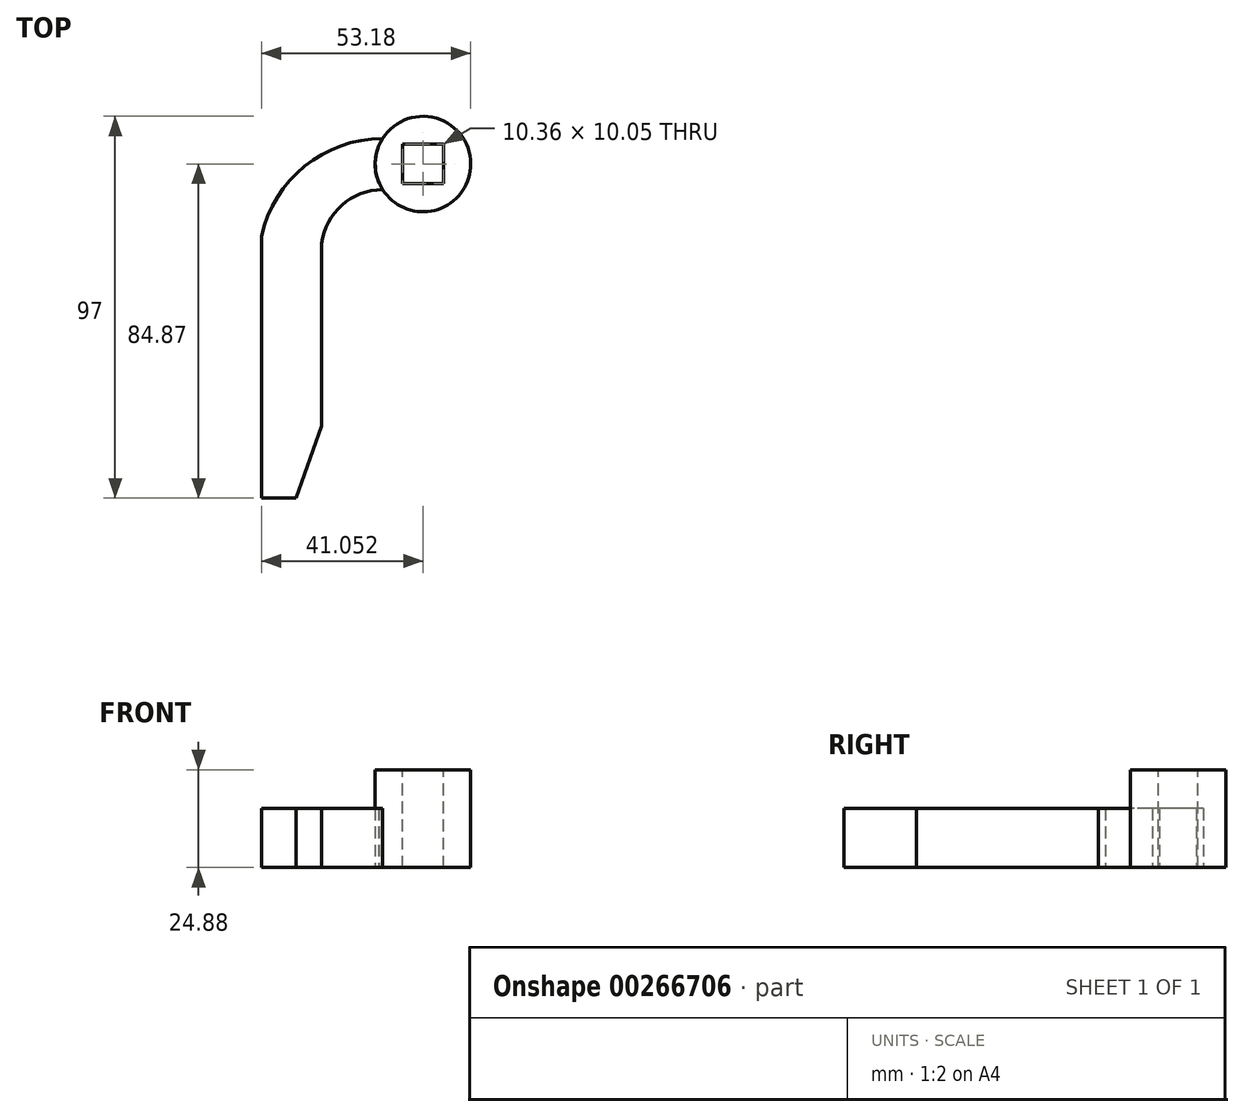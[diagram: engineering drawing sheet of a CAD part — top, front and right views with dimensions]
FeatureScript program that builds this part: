
annotation { "Feature Type Name" : "Feature", "Feature Type Description" : "" }
export const myFeature = defineFeature(function(context is Context, id is Id, definition is map)
    precondition{}
    {
        {
            var Q0;
            Q0=qCreatedBy(makeId("Top.planeOp"),FACE);
            var sketch = newSketch(context, id + "F0", { "sketchPlane" : qUnion([Q0])});
            skCircle(sketch, "E0", {"center": v(50.95, 0) * mm, "radius": 12.13 * mm});
            skSolve(sketch);
        }
        {
            var Q0;
            Q0=qCreatedBy(makeId("Top.planeOp"),FACE);
            var sketch = newSketch(context, id + "F1", { "sketchPlane" : qUnion([Q0])});
            skLineSegment(sketch, "E1.bottom", {"start": v(40.74, 6.47) * mm, "end": v(40.72, 6.47) * mm});
            skLineSegment(sketch, "E1.top", {"start": v(40.75, -6.48) * mm, "end": v(40.74, -6.48) * mm});
            skArc(sketch, "E2", {"start": v(40.74, 6.47) * mm, "mid": v(20.92, -0.54) * mm, "end": v(9.9, -18.45) * mm});
            skArc(sketch, "E3", {"start": v(40.74, -6.48) * mm, "mid": v(30.36, -10.42) * mm, "end": v(25.2, -20.25) * mm});
            skLineSegment(sketch, "E4", {"start": v(25.2, -20.25) * mm, "end": v(25.2, -66.54) * mm});
            skLineSegment(sketch, "E5", {"start": v(9.9, -18.45) * mm, "end": v(9.9, -84.87) * mm});
            skLineSegment(sketch, "E6", {"start": v(9.9, -84.87) * mm, "end": v(18.7, -84.87) * mm});
            skLineSegment(sketch, "E7", {"start": v(18.7, -84.87) * mm, "end": v(25.2, -66.54) * mm});
            skArc(sketch, "E8", {"start": v(40.74, 6.47) * mm, "mid": v(38.78, 0) * mm, "end": v(40.75, -6.48) * mm});
            skSolve(sketch);
        }
        {
            var Q0;
            Q0=makeQuery(id+"F0.imprint","IMPRINT",FACE,{"disambiguationData":[TD([[makeQuery(id+"F0.imprint","IMPRINT",EDGE,{"derivedFrom":sQuery(id+"F0.wireOp",EDGE,"E0")}),1.0]])]});
            extrude(context, id + "F2", {"entities" : qUnion([Q0]), "depth" : 24.88 * mm});
        }
        {
            var Q0;
            Q0=makeQuery(id+"F2.opExtrude","CAP_FACE",FACE,{"disambiguationData":[OSD([sQuery(id+"F0.wireOp",EDGE,"E0")])],"isStart":false});
            var sketch = newSketch(context, id + "F3", { "sketchPlane" : qUnion([Q0])});
            skLineSegment(sketch, "E9.bottom", {"start": v(56.13, 5.03) * mm, "end": v(45.77, 5.03) * mm});
            skLineSegment(sketch, "E9.top", {"start": v(56.13, -5.03) * mm, "end": v(45.77, -5.03) * mm});
            skLineSegment(sketch, "E9.left", {"start": v(56.13, 5.03) * mm, "end": v(56.13, -5.03) * mm});
            skLineSegment(sketch, "E9.right", {"start": v(45.77, 5.03) * mm, "end": v(45.77, -5.03) * mm});
            skPoint(sketch, "E9.middle", {"position": v(50.95, 0) * mm});
            skSolve(sketch);
        }
        {
            var Q0;
            Q0 = qSketchRegion(id + "F3", true);
            extrude(context, id + "F4", {"entities" : qUnion([Q0]), "operationType" : NewBodyOperationType.REMOVE, "oppositeDirection" : true, "depth" : 25 * mm});
        }
        {
            var Q0;
            Q0=makeQuery(id+"F1.imprint","IMPRINT",FACE,{"disambiguationData":[TD([[makeQuery(id+"F1.imprint","IMPRINT",EDGE,{"derivedFrom":sQuery(id+"F1.wireOp",EDGE,"E1.top")}),-1.0]])]});
            extrude(context, id + "F5", {"entities" : qUnion([Q0]), "operationType" : NewBodyOperationType.ADD, "depth" : 15 * mm});
        }
    });
